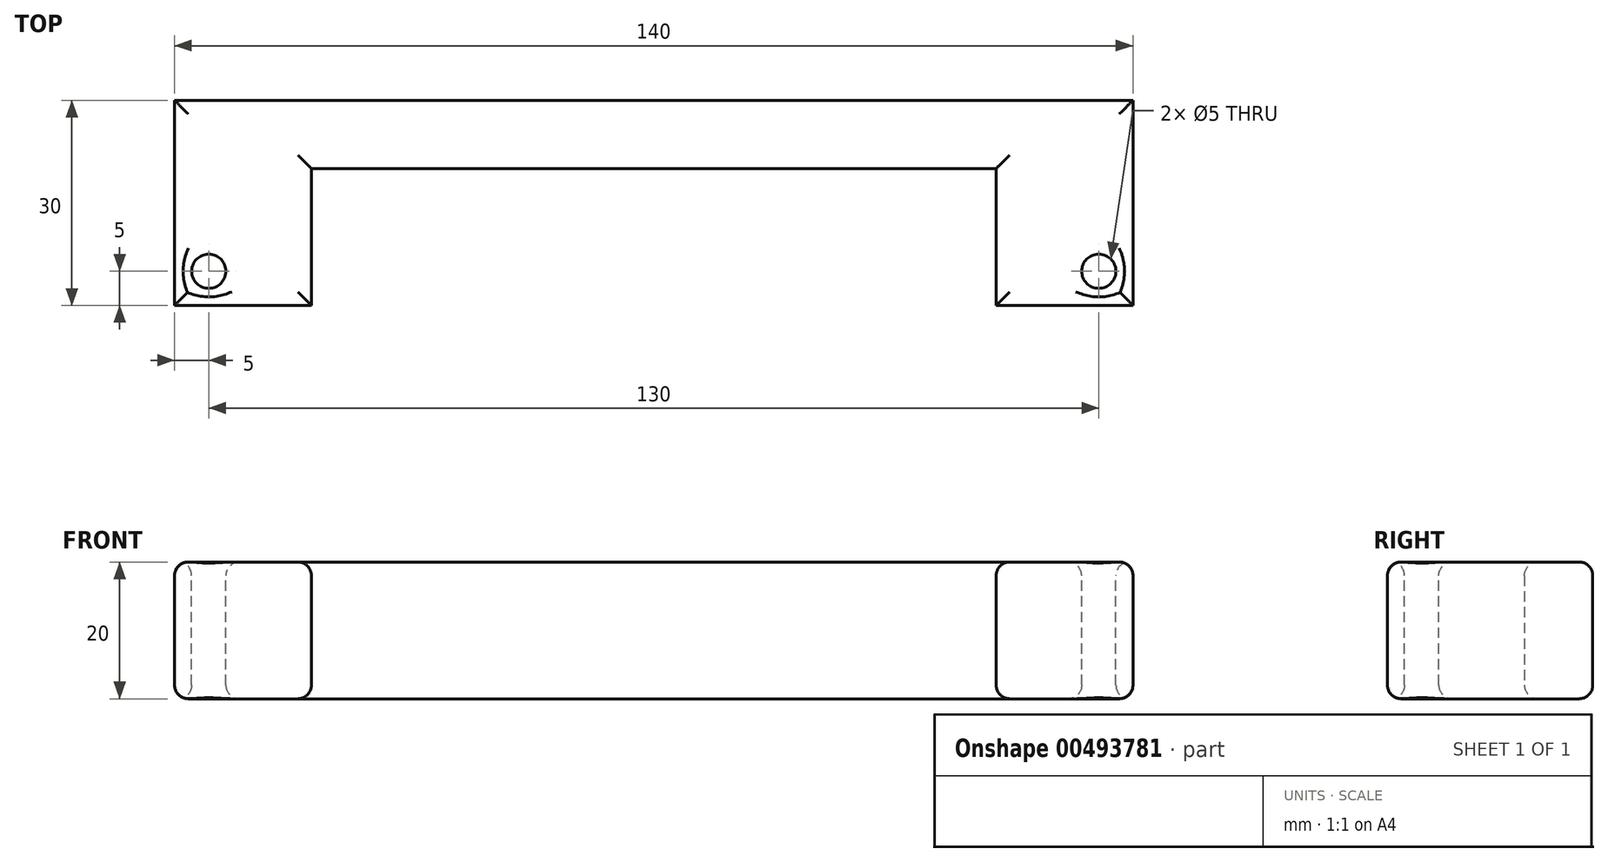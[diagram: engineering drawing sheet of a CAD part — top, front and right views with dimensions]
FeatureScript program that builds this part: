
annotation { "Feature Type Name" : "Feature", "Feature Type Description" : "" }
export const myFeature = defineFeature(function(context is Context, id is Id, definition is map)
    precondition{}
    {
        {
            var Q0;
            Q0=qCreatedBy(makeId("Top.planeOp"),FACE);
            var sketch = newSketch(context, id + "F0", { "sketchPlane" : qUnion([Q0])});
            skLineSegment(sketch, "E0", {"start": v(0, 30) * mm, "end": v(0, 20) * mm});
            skLineSegment(sketch, "E1", {"start": v(0, 20) * mm, "end": v(50, 20) * mm});
            skLineSegment(sketch, "E2", {"start": v(50, 20) * mm, "end": v(50, 0) * mm});
            skLineSegment(sketch, "E3", {"start": v(50, 0) * mm, "end": v(70, 0) * mm});
            skLineSegment(sketch, "E4", {"start": v(70, 0) * mm, "end": v(70, 30) * mm});
            skLineSegment(sketch, "E5", {"start": v(70, 30) * mm, "end": v(0, 30) * mm});
            skSolve(sketch);
        }
        {
            var Q0;
            Q0 = qSketchRegion(id + "F0", true);
            extrude(context, id + "F1", {"entities" : qUnion([Q0]), "depth" : 20 * mm});
        }
        {
            var Q0;
            Q0=makeQuery(id+"F1.opExtrude","CAP_FACE",FACE,{"disambiguationData":[OSD([sQuery(id+"F0.wireOp",EDGE,"E0"),sQuery(id+"F0.wireOp",EDGE,"E1"),sQuery(id+"F0.wireOp",EDGE,"E2"),sQuery(id+"F0.wireOp",EDGE,"E3"),sQuery(id+"F0.wireOp",EDGE,"E4"),sQuery(id+"F0.wireOp",EDGE,"E5")])],"isStart":false});
            var sketch = newSketch(context, id + "F2", { "sketchPlane" : qUnion([Q0])});
            skPoint(sketch, "E6", {"position": v(65, 5) * mm});
            skSolve(sketch);
        }
        {
            var Q0;
            Q0=sQuery(id+"F2.wireOp",VERTEX,"E6");
            var Q1;
            Q1=makeQuery(id+"F1.opExtrude","SWEPT_BODY",BODY,{"disambiguationData":[OSD([sQuery(id+"F0.wireOp",EDGE,"E0"),sQuery(id+"F0.wireOp",EDGE,"E1"),sQuery(id+"F0.wireOp",EDGE,"E2"),sQuery(id+"F0.wireOp",EDGE,"E3"),sQuery(id+"F0.wireOp",EDGE,"E4"),sQuery(id+"F0.wireOp",EDGE,"E5")])]});
            hole(context, id + "F3", {"style" : HoleStyle.SIMPLE, "endStyle" : HoleEndStyle.THROUGH, "holeDiameter" : 5 * mm, "isTappedThrough" : true, "tappedDepth" : 12 * mm, "tapClearance" : 3, "locations" : qUnion([Q0]), "scope" : qUnion([Q1])});
        }
        {
            var Q0;
            Q0=makeQuery(id+"F1.opExtrude","SWEPT_BODY",BODY,{"disambiguationData":[OSD([sQuery(id+"F0.wireOp",EDGE,"E0"),sQuery(id+"F0.wireOp",EDGE,"E1"),sQuery(id+"F0.wireOp",EDGE,"E2"),sQuery(id+"F0.wireOp",EDGE,"E3"),sQuery(id+"F0.wireOp",EDGE,"E4"),sQuery(id+"F0.wireOp",EDGE,"E5")])]});
            var Q1;
            Q1=makeQuery(id+"F1.opExtrude","SWEPT_FACE",FACE,{"disambiguationData":[OSD([sQuery(id+"F0.wireOp",EDGE,"E0")])]});
            mirror(context, id + "F4", {"operationType" : NewBodyOperationType.ADD, "entities" : qUnion([Q0]), "mirrorPlane" : qUnion([Q1])});
        }
        {
            var Q0;
            {var subQ0=makeQuery(id+"F1.opExtrude","CAP_FACE",FACE,{"disambiguationData":[OSD([sQuery(id+"F0.wireOp",EDGE,"E0"),sQuery(id+"F0.wireOp",EDGE,"E1"),sQuery(id+"F0.wireOp",EDGE,"E2"),sQuery(id+"F0.wireOp",EDGE,"E3"),sQuery(id+"F0.wireOp",EDGE,"E4"),sQuery(id+"F0.wireOp",EDGE,"E5")])],"isStart":true});Q0=makeQuery(id+"F4.boolean.opBoolean","MERGE",FACE,{"derivedFrom":[subQ0,makeQuery(id+"F4.opPattern","COPY",FACE,{"derivedFrom":subQ0,"instanceName":"1"})]});}
            var Q1;
            {var subQ0=makeQuery(id+"F1.opExtrude","CAP_FACE",FACE,{"disambiguationData":[OSD([sQuery(id+"F0.wireOp",EDGE,"E0"),sQuery(id+"F0.wireOp",EDGE,"E1"),sQuery(id+"F0.wireOp",EDGE,"E2"),sQuery(id+"F0.wireOp",EDGE,"E3"),sQuery(id+"F0.wireOp",EDGE,"E4"),sQuery(id+"F0.wireOp",EDGE,"E5")])],"isStart":false});Q1=makeQuery(id+"F4.boolean.opBoolean","MERGE",FACE,{"derivedFrom":[subQ0,makeQuery(id+"F4.opPattern","COPY",FACE,{"derivedFrom":subQ0,"instanceName":"1"})]});}
            fillet(context, id + "F5", {"entities" : qUnion([Q0, Q1]), "radius" : 2 * mm, "tangentPropagation" : true, "allowEdgeOverflow" : false});
        }
    });
